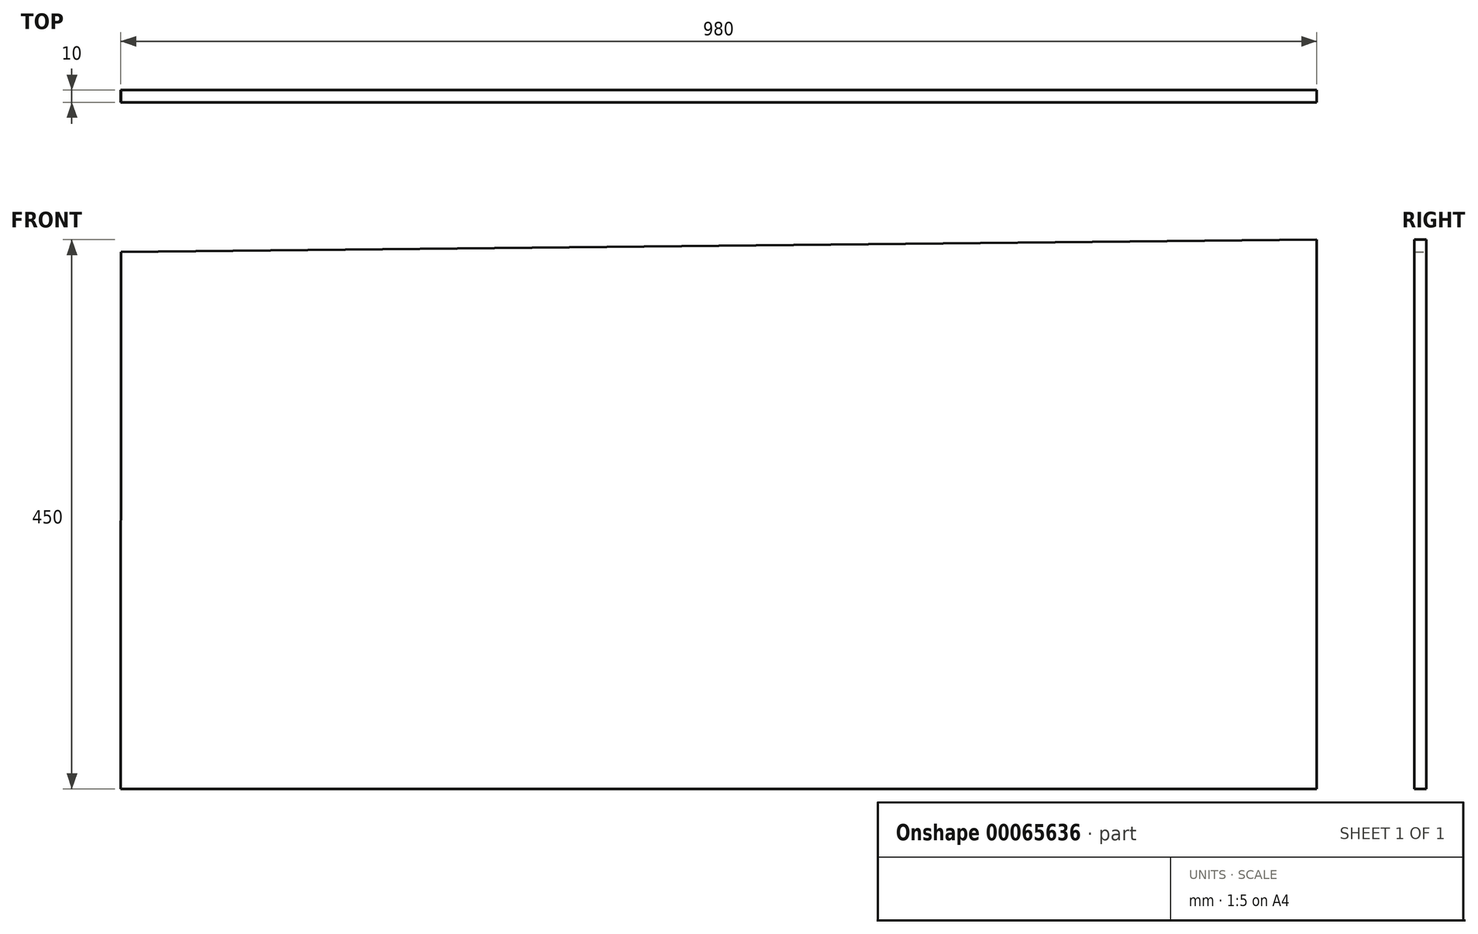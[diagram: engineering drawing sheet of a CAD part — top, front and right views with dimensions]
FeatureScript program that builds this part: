
annotation { "Feature Type Name" : "Feature", "Feature Type Description" : "" }
export const myFeature = defineFeature(function(context is Context, id is Id, definition is map)
    precondition{}
    {
        {
            var Q0;
            Q0=qCreatedBy(makeId("Front.planeOp"),FACE);
            var sketch = newSketch(context, id + "F0", { "sketchPlane" : qUnion([Q0])});
            skLineSegment(sketch, "E0", {"start": v(-980, 0) * mm, "end": v(0, 0) * mm});
            skLineSegment(sketch, "E1", {"start": v(0, 0) * mm, "end": v(0, 450) * mm});
            skLineSegment(sketch, "E2", {"start": v(0, 450) * mm, "end": v(-979.95, 440) * mm});
            skLineSegment(sketch, "E3", {"start": v(-979.95, 440) * mm, "end": v(-980, 0) * mm});
            skLineSegment(sketch, "E4", {"start": v(-670, 0) * mm, "end": v(-670, 443.16) * mm});
            skLineSegment(sketch, "E5", {"start": v(-310, 0) * mm, "end": v(-310, 446.84) * mm});
            skSolve(sketch);
        }
        {
            var Q0;
            Q0 = qSketchRegion(id + "F0", true);
            extrude(context, id + "F1", {"entities" : qUnion([Q0]), "depth" : 10 * mm});
        }
    });
